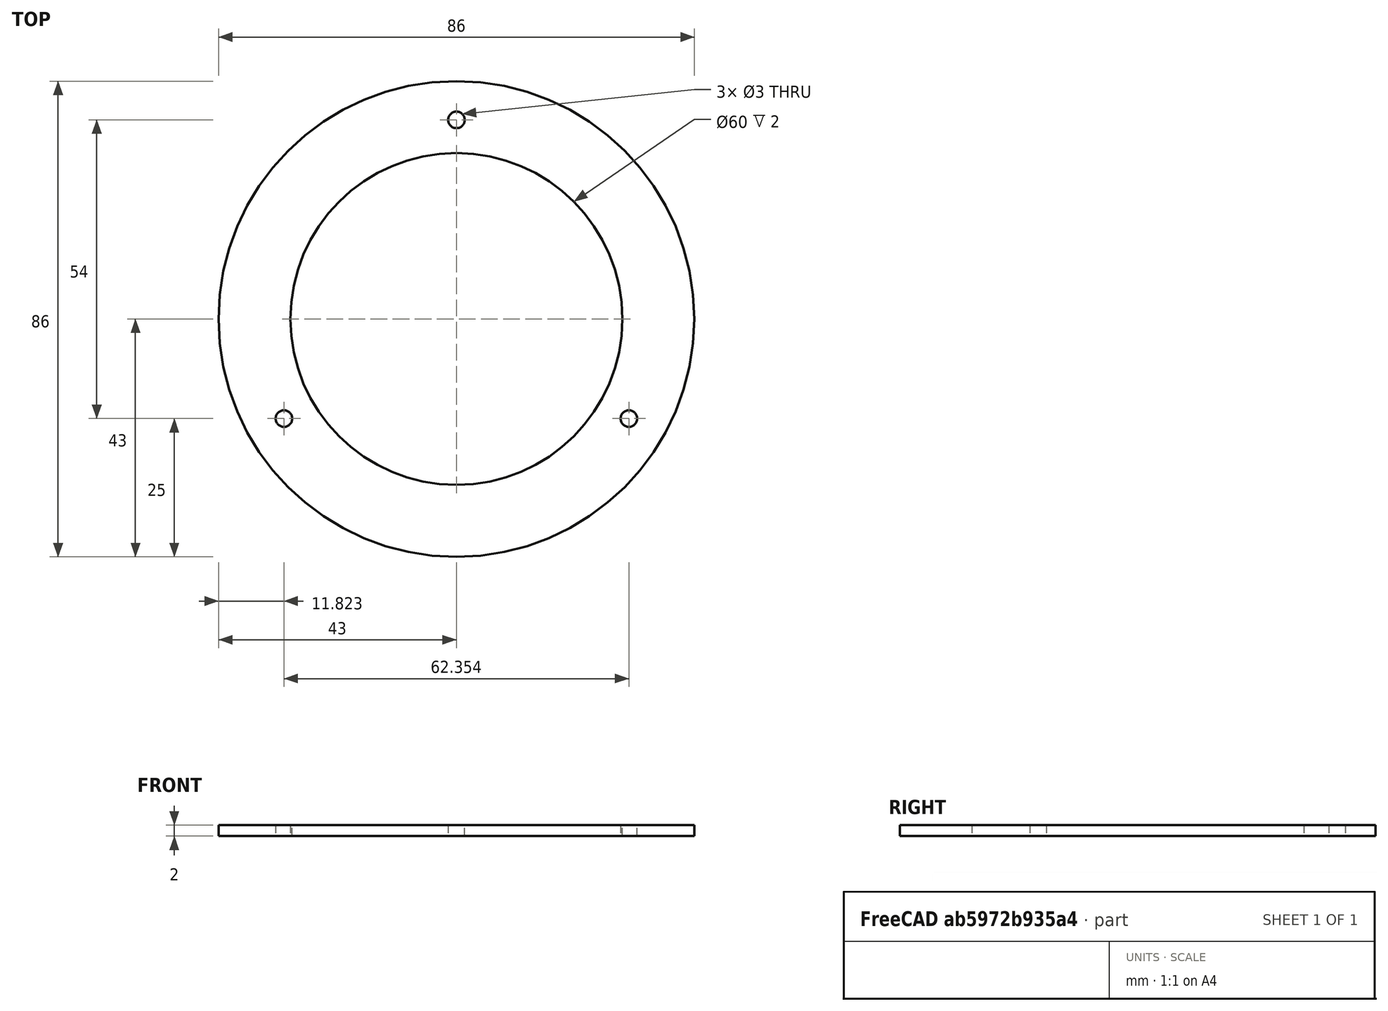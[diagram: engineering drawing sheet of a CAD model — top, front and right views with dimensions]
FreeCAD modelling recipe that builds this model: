
FCSTD DOCUMENT  (FreeCAD 0.19R24276 (Git))
Label: Ring_underglass_h_2_0mm_V6
License: All rights reserved
LicenseURL: http://en.wikipedia.org/wiki/All_rights_reserved
objects: Sketcher::SketchObject×1, PartDesign::Pad×1, PartDesign::Body×1
note: 4 computed .brp shape members not serialized (recipe doc carries the construction recipe); baked Part::Feature solids carry a one-line shape summary decoded from their .brp

FEATURE [Sketcher::SketchObject] Sketch006  label="Sketch006_d72_3_otv_d3"
  FullyConstrained = true
  MapMode = 5
  Placement = pos=(0,0,22) rot=(0,0,1;0rad)
  sketch-geometry (9):
    g0: LineSegment StartX=0 StartY=36 StartZ=0 EndX=-31.1769 EndY=-18 EndZ=0
    g1: LineSegment StartX=-31.1769 StartY=-18 StartZ=0 EndX=31.1769 EndY=-18 EndZ=0
    g2: LineSegment StartX=31.1769 StartY=-18 StartZ=0 EndX=0 EndY=36 EndZ=0
    g3: Circle CenterX=0 CenterY=0 CenterZ=0 NormalX=0 NormalY=0 NormalZ=1 AngleXU=0 Radius=36
    g4: Circle CenterX=0 CenterY=36 CenterZ=0 NormalX=0 NormalY=0 NormalZ=1 AngleXU=0 Radius=1.5
    g5: Circle CenterX=31.1769 CenterY=-18 CenterZ=0 NormalX=0 NormalY=0 NormalZ=1 AngleXU=0 Radius=1.5
    g6: Circle CenterX=-31.1769 CenterY=-18 CenterZ=0 NormalX=0 NormalY=0 NormalZ=1 AngleXU=0 Radius=1.5
    g7: Circle CenterX=0 CenterY=0 CenterZ=0 NormalX=0 NormalY=0 NormalZ=1 AngleXU=0 Radius=43
    g8: Circle CenterX=0 CenterY=0 CenterZ=0 NormalX=0 NormalY=0 NormalZ=1 AngleXU=0 Radius=30
  constraints (21):
    c: Coincident(g0,g1)
    c: Coincident(g1,g2)
    c: Coincident(g2,g0)
    c: Equal(g0,g1)
    c: Equal(g0,g2)
    c: PointOnObject(g0,g3)
    c: PointOnObject(g1,g3)
    c: PointOnObject(g2,g3)
    c: Coincident(g3,g-1)
    c: PointOnObject(g2,g-2)
    c: Diameter(g3) = 72
    c: Coincident(g4,g0)
    c: Coincident(g5,g1)
    c: Coincident(g6,g0)
    c: Diameter(g6) = 3
    c: Equal(g6,g4)
    c: Equal(g6,g5)
    c: Coincident(g7,g-1)
    c: Diameter(g7) = 86
    c: Coincident(g8,g7)
    c: Diameter(g8) = 60
FEATURE [PartDesign::Pad] Pad  label="Pad_h3"
  Direction = (1,1,1)
  Length = 2
  Length2 = 100
  Placement = pos=(0,0,22) rot=(0,0,1;0rad)
  Profile = -> Sketch006
  Type = 0
FEATURE [PartDesign::Body] Body
  Group = -> [Sketch006,Pad]
  Origin = -> Origin
  Tip = -> Pad
